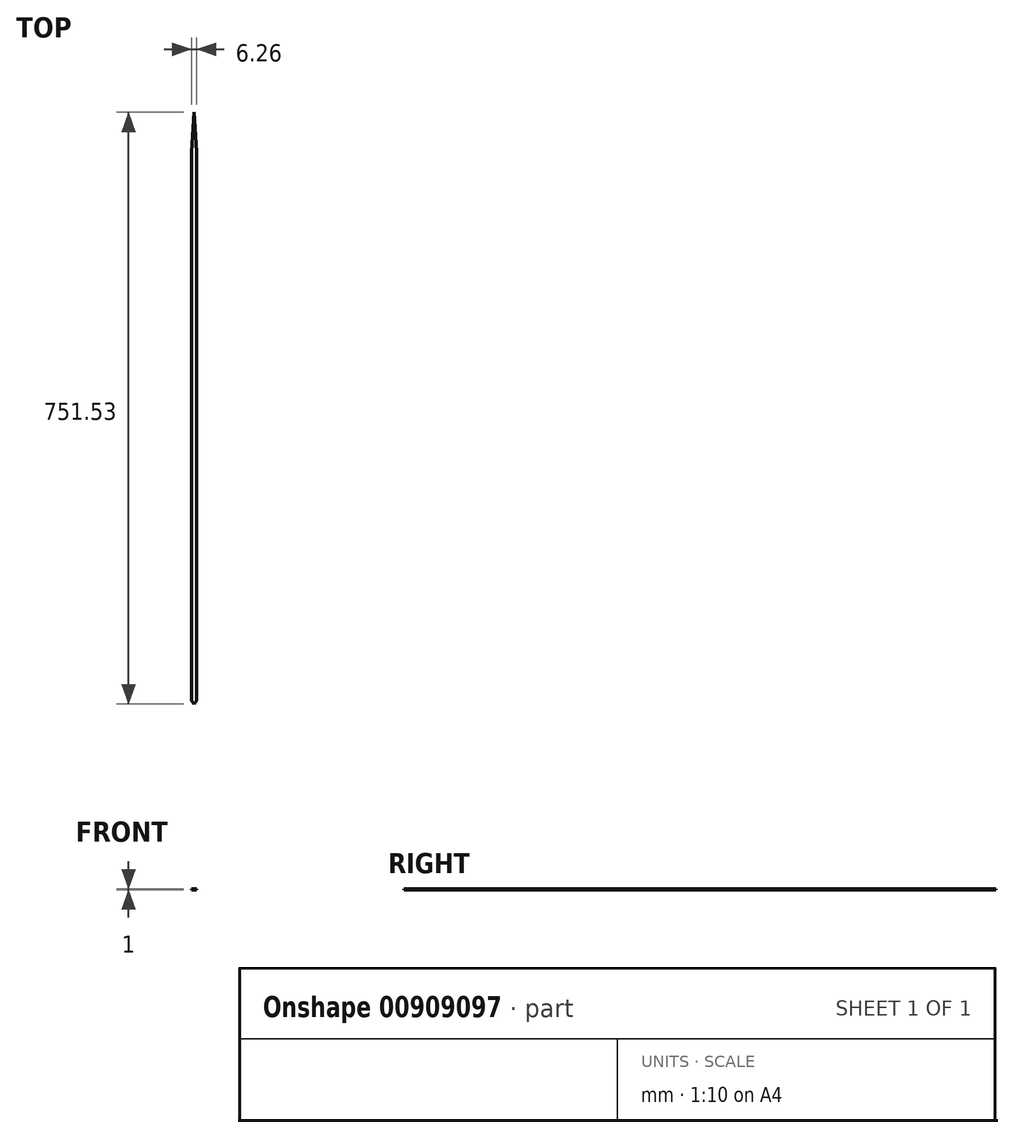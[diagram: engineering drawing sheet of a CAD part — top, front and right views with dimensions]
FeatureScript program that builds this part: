
annotation { "Feature Type Name" : "Feature", "Feature Type Description" : "" }
export const myFeature = defineFeature(function(context is Context, id is Id, definition is map)
    precondition{}
    {
        {
            var Q0;
            Q0=qCreatedBy(makeId("Front.planeOp"),FACE);
            cPlane(context, id + "F0", {"entities" : qUnion([Q0]), "cplaneType" : CPlaneType.OFFSET, "offset" : 50 * mm, "width" : 150 * mm, "height" : 150 * mm});
        }
        {
            var Q0;
            Q0=qCreatedBy(id+"F0.planeOp",FACE);
            cPlane(context, id + "F1", {"entities" : qUnion([Q0]), "cplaneType" : CPlaneType.OFFSET, "offset" : 43 * mm, "width" : 150 * mm, "height" : 150 * mm});
        }
        {
            var Q0;
            Q0=qCreatedBy(id+"F1.planeOp",FACE);
            cPlane(context, id + "F2", {"entities" : qUnion([Q0]), "cplaneType" : CPlaneType.OFFSET, "offset" : 77 * mm, "width" : 150 * mm, "height" : 150 * mm});
        }
        {
            var Q0;
            Q0=qCreatedBy(id+"F2.planeOp",FACE);
            cPlane(context, id + "F3", {"entities" : qUnion([Q0]), "cplaneType" : CPlaneType.OFFSET, "offset" : 77 * mm, "width" : 150 * mm, "height" : 150 * mm});
        }
        {
            var Q0;
            Q0=qCreatedBy(id+"F3.planeOp",FACE);
            cPlane(context, id + "F4", {"entities" : qUnion([Q0]), "cplaneType" : CPlaneType.OFFSET, "offset" : 74 * mm, "width" : 150 * mm, "height" : 150 * mm});
        }
        {
            var Q0;
            Q0=qCreatedBy(id+"F4.planeOp",FACE);
            cPlane(context, id + "F5", {"entities" : qUnion([Q0]), "cplaneType" : CPlaneType.OFFSET, "offset" : 74 * mm, "width" : 150 * mm, "height" : 150 * mm});
        }
        {
            var Q0;
            Q0=qCreatedBy(id+"F5.planeOp",FACE);
            cPlane(context, id + "F6", {"entities" : qUnion([Q0]), "cplaneType" : CPlaneType.OFFSET, "offset" : 74 * mm, "width" : 150 * mm, "height" : 150 * mm});
        }
        {
            var Q0;
            Q0=qCreatedBy(id+"F6.planeOp",FACE);
            cPlane(context, id + "F7", {"entities" : qUnion([Q0]), "cplaneType" : CPlaneType.OFFSET, "offset" : 74 * mm, "width" : 150 * mm, "height" : 150 * mm});
        }
        {
            var Q0;
            Q0=qCreatedBy(id+"F7.planeOp",FACE);
            cPlane(context, id + "F8", {"entities" : qUnion([Q0]), "cplaneType" : CPlaneType.OFFSET, "offset" : 72 * mm, "width" : 150 * mm, "height" : 150 * mm});
        }
        {
            var Q0;
            Q0=qCreatedBy(id+"F8.planeOp",FACE);
            cPlane(context, id + "F9", {"entities" : qUnion([Q0]), "cplaneType" : CPlaneType.OFFSET, "offset" : 75 * mm, "width" : 150 * mm, "height" : 150 * mm});
        }
        {
            var Q0;
            Q0=qCreatedBy(id+"F9.planeOp",FACE);
            cPlane(context, id + "F10", {"entities" : qUnion([Q0]), "cplaneType" : CPlaneType.OFFSET, "offset" : 37 * mm, "width" : 150 * mm, "height" : 150 * mm});
        }
        {
            var Q0;
            Q0=qCreatedBy(id+"F10.planeOp",FACE);
            cPlane(context, id + "F11", {"entities" : qUnion([Q0]), "cplaneType" : CPlaneType.OFFSET, "offset" : 37 * mm, "width" : 150 * mm, "height" : 150 * mm});
        }
        {
            var Q0;
            Q0=qCreatedBy(makeId("Top.planeOp"),FACE);
            cPlane(context, id + "F12", {"entities" : qUnion([Q0]), "cplaneType" : CPlaneType.OFFSET, "offset" : 76 * mm, "oppositeDirection" : true, "width" : 150 * mm, "height" : 150 * mm});
        }
        {
            var Q0;
            Q0=qCreatedBy(id+"F12.planeOp",FACE);
            var sketch = newSketch(context, id + "F13", { "sketchPlane" : qUnion([Q0])});
            skLineSegment(sketch, "E0", {"start": v(0, 0) * mm, "end": v(-3.13, -50) * mm});
            skLineSegment(sketch, "E1", {"start": v(-3.13, -50) * mm, "end": v(-3.13, -747.99) * mm});
            skLineSegment(sketch, "E2", {"start": v(-3.13, -747.99) * mm, "end": v(0, -751.53) * mm});
            skLineSegment(sketch, "E3", {"start": v(0, -751.53) * mm, "end": v(0, 0) * mm});
            skSolve(sketch);
        }
        {
            var Q0;
            Q0 = qSketchRegion(id + "F13", true);
            extrude(context, id + "F14", {"entities" : qUnion([Q0]), "oppositeDirection" : true, "depth" : 1 * mm, "offsetDistance" : 25 * mm});
        }
        {
            var Q0;
            Q0=makeQuery(id+"F14.opExtrude","SWEPT_BODY",BODY,{"disambiguationData":[OSD([sQuery(id+"F13.wireOp",EDGE,"E0"),sQuery(id+"F13.wireOp",EDGE,"E1"),sQuery(id+"F13.wireOp",EDGE,"E2"),sQuery(id+"F13.wireOp",EDGE,"E3")])]});
            var Q1;
            Q1=makeQuery(id+"F14.opExtrude","SWEPT_FACE",FACE,{"disambiguationData":[OSD([sQuery(id+"F13.wireOp",EDGE,"E3")])]});
            mirror(context, id + "F15", {"operationType" : NewBodyOperationType.ADD, "entities" : qUnion([Q0]), "mirrorPlane" : qUnion([Q1])});
        }
    });
